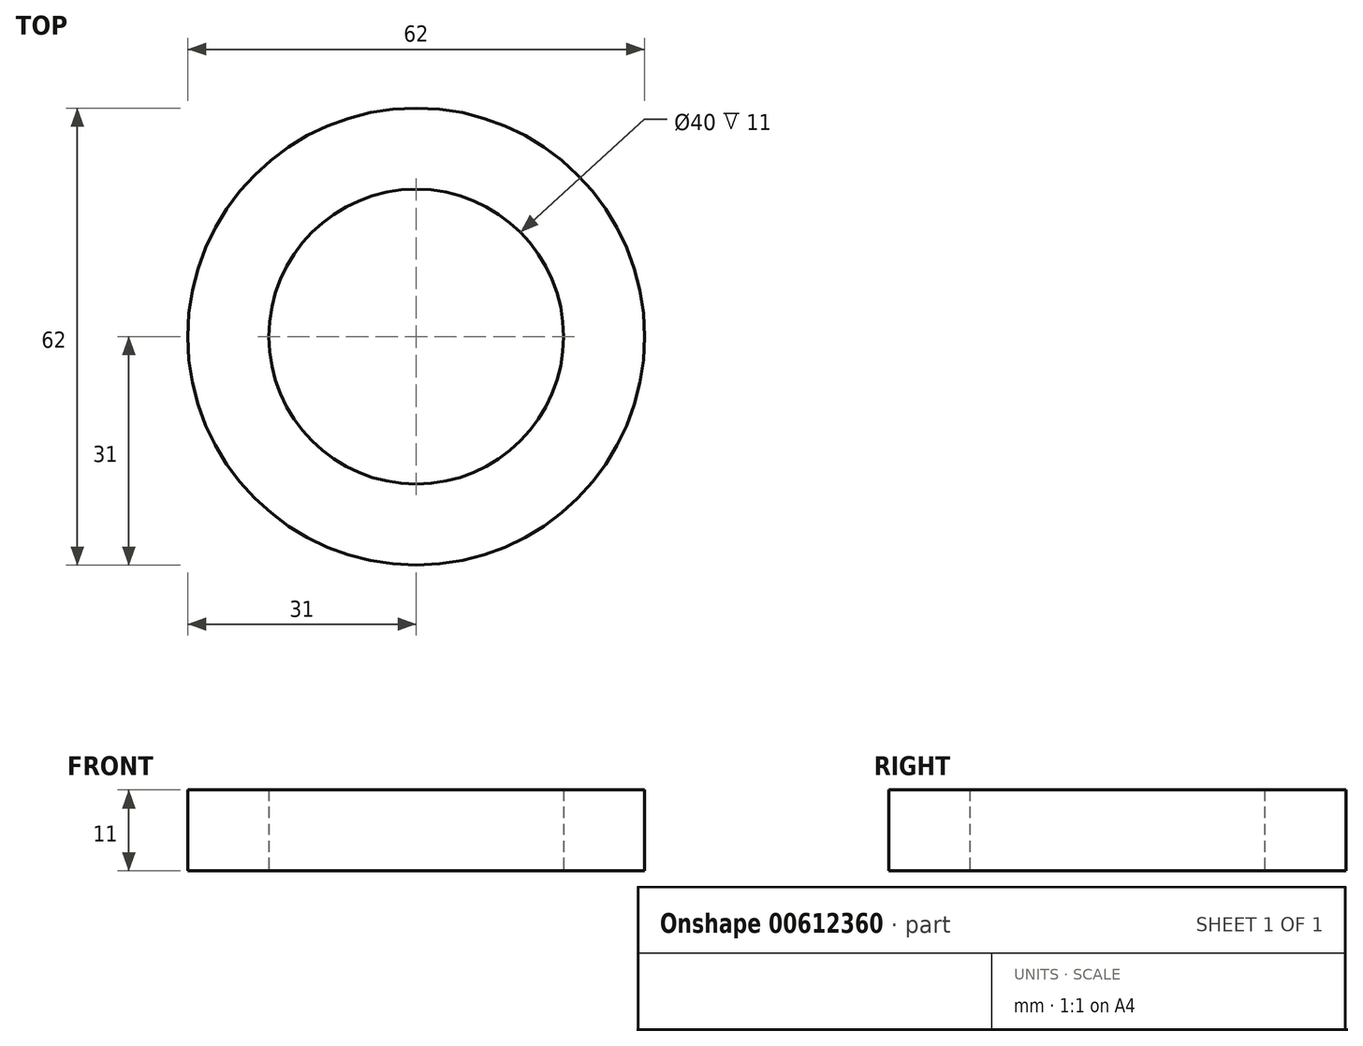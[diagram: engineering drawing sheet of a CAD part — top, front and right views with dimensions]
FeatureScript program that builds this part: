
annotation { "Feature Type Name" : "Feature", "Feature Type Description" : "" }
export const myFeature = defineFeature(function(context is Context, id is Id, definition is map)
    precondition{}
    {
        {
            var Q0;
            Q0=qCreatedBy(makeId("Front.planeOp"),FACE);
            var sketch = newSketch(context, id + "F0", { "sketchPlane" : qUnion([Q0])});
            skLineSegment(sketch, "E0.bottom", {"start": v(20, 0) * mm, "end": v(31, 0) * mm});
            skLineSegment(sketch, "E0.top", {"start": v(20, 11) * mm, "end": v(31, 11) * mm});
            skLineSegment(sketch, "E0.left", {"start": v(20, 0) * mm, "end": v(20, 11) * mm});
            skLineSegment(sketch, "E0.right", {"start": v(31, 0) * mm, "end": v(31, 11) * mm});
            skLineSegment(sketch, "E1", {"start": v(0, 0) * mm, "end": v(0, 16.93) * mm});
            skSolve(sketch);
        }
        {
            var Q0;
            Q0=makeQuery(id+"F0.imprint","IMPRINT",FACE,{"disambiguationData":[TD([[makeQuery(id+"F0.imprint","IMPRINT",EDGE,{"derivedFrom":sQuery(id+"F0.wireOp",EDGE,"E0.bottom")}),1.0]])]});
            var Q1;
            Q1=sQuery(id+"F0.wireOp",EDGE,"E1");
            revolve(context, id + "F1", {"entities" : qUnion([Q0]), "axis" : qUnion([Q1]), "revolveType" : RevolveType.FULL});
        }
    });
